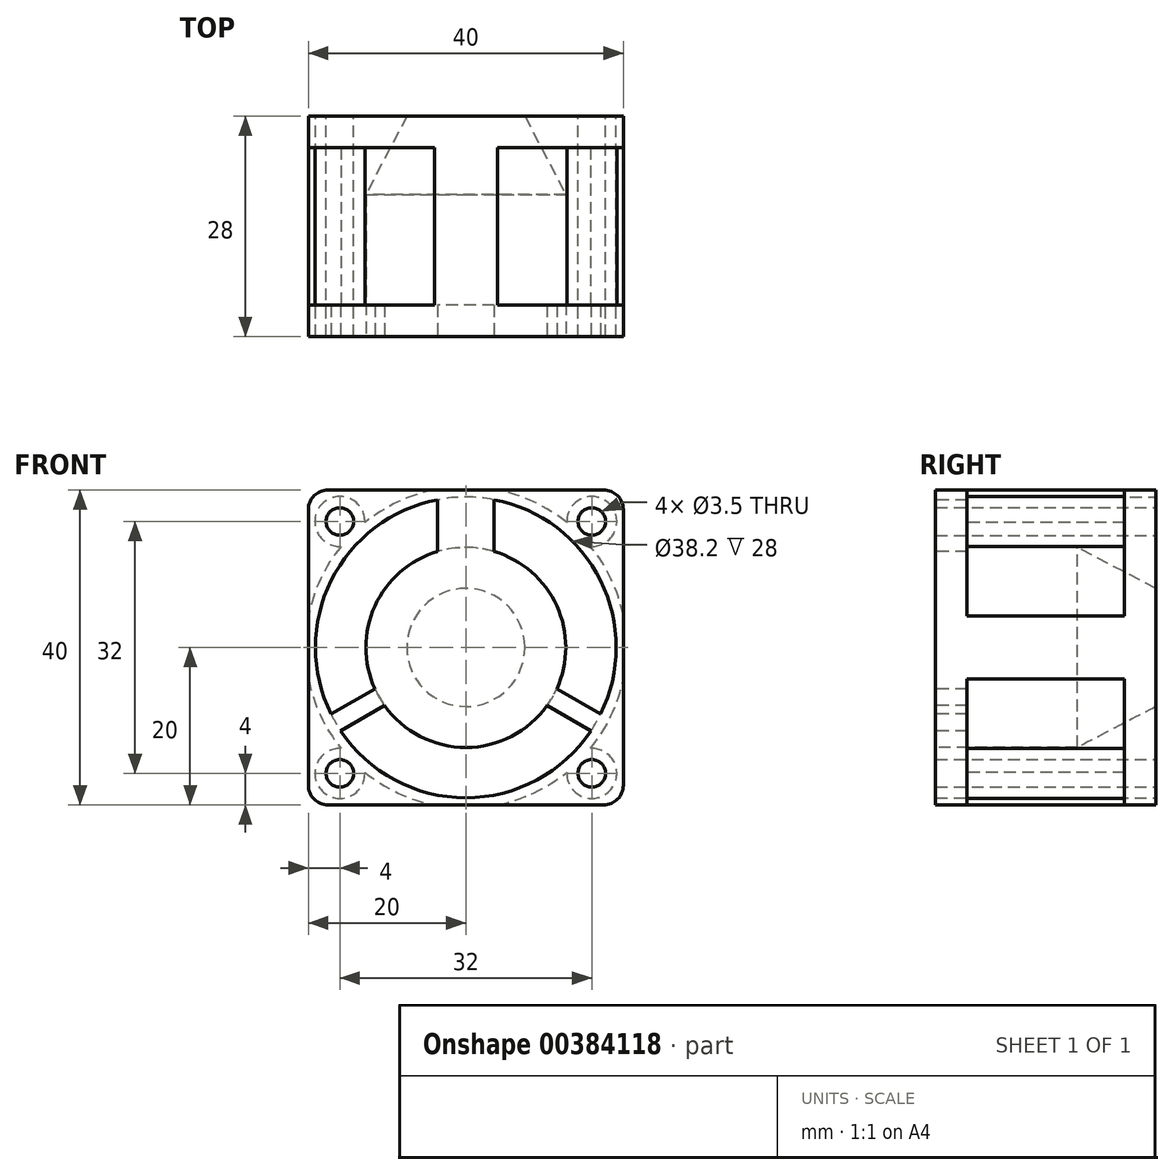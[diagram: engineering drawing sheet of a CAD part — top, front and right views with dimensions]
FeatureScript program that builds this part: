
annotation { "Feature Type Name" : "Feature", "Feature Type Description" : "" }
export const myFeature = defineFeature(function(context is Context, id is Id, definition is map)
    precondition{}
    {
        {
            var Q0;
            Q0=qCreatedBy(makeId("Front.planeOp"),FACE);
            var sketch = newSketch(context, id + "F0", { "sketchPlane" : qUnion([Q0])});
            skLineSegment(sketch, "E0.bottom", {"start": v(-20, 20) * mm, "end": v(20, 20) * mm});
            skLineSegment(sketch, "E0.top", {"start": v(-20, -20) * mm, "end": v(20, -20) * mm});
            skLineSegment(sketch, "E0.left", {"start": v(-20, 20) * mm, "end": v(-20, -20) * mm});
            skLineSegment(sketch, "E0.right", {"start": v(20, 20) * mm, "end": v(20, -20) * mm});
            skLineSegment(sketch, "E1", {"start": v(0, 22.42) * mm, "end": v(0, -25.75) * mm, "construction": true});
            skLineSegment(sketch, "E2", {"start": v(-21.61, 0) * mm, "end": v(23.43, 0) * mm, "construction": true});
            skLineSegment(sketch, "E3", {"start": v(-20.42, 20.42) * mm, "end": v(24.04, -24.04) * mm, "construction": true});
            skLineSegment(sketch, "E4", {"start": v(22.41, 22.41) * mm, "end": v(-20.4, -20.4) * mm, "construction": true});
            skCircle(sketch, "E5", {"center": v(-16, 16) * mm, "radius": 1.75 * mm});
            skCircle(sketch, "E6", {"center": v(16, 16) * mm, "radius": 1.75 * mm});
            skCircle(sketch, "E7", {"center": v(16, -16) * mm, "radius": 1.75 * mm});
            skCircle(sketch, "E8", {"center": v(-16, -16) * mm, "radius": 1.75 * mm});
            skCircle(sketch, "E9", {"center": v(0, 0) * mm, "radius": 19.1 * mm});
            skSolve(sketch);
        }
        {
            var Q0;
            Q0=qSketchRegion(id+"F0",true);
            extrude(context, id + "F1", {"entities" : qUnion([Q0]), "depth" : 28 * mm, "symmetric" : true});
        }
        {
            var Q0;
            Q0=qCreatedBy(makeId("Front.planeOp"),FACE);
            var sketch = newSketch(context, id + "F2", { "sketchPlane" : qUnion([Q0])});
            skArc(sketch, "E10", {"start": v(-12.83, 15.86) * mm, "mid": v(-18.25, 18.25) * mm, "end": v(-15.86, 12.83) * mm});
            skArc(sketch, "E11", {"start": v(-15.86, 12.83) * mm, "mid": v(-18.46, 8.67) * mm, "end": v(-20, 4) * mm});
            skLineSegment(sketch, "E12", {"start": v(20.4, 20.4) * mm, "end": v(4, 20.4) * mm});
            skLineSegment(sketch, "E13", {"start": v(-20.4, 20.4) * mm, "end": v(-20.4, 4) * mm});
            skLineSegment(sketch, "E14", {"start": v(-20.4, -20.4) * mm, "end": v(-4, -20.4) * mm});
            skLineSegment(sketch, "E15", {"start": v(20.4, -20.4) * mm, "end": v(20.4, -4) * mm});
            skArc(sketch, "E16", {"start": v(15.86, 12.83) * mm, "mid": v(18.25, 18.25) * mm, "end": v(12.83, 15.86) * mm});
            skArc(sketch, "E17", {"start": v(12.83, -15.86) * mm, "mid": v(18.25, -18.25) * mm, "end": v(15.86, -12.83) * mm});
            skArc(sketch, "E18", {"start": v(-15.86, -12.83) * mm, "mid": v(-18.25, -18.25) * mm, "end": v(-12.83, -15.86) * mm});
            skArc(sketch, "E19.trimOffspring", {"start": v(12.83, 15.86) * mm, "mid": v(8.67, 18.46) * mm, "end": v(4, 20) * mm});
            skArc(sketch, "E20.trimOffspring", {"start": v(15.86, -12.83) * mm, "mid": v(18.46, -8.67) * mm, "end": v(20, -4) * mm});
            skArc(sketch, "E21.trimOffspring", {"start": v(-12.83, -15.86) * mm, "mid": v(-8.67, -18.46) * mm, "end": v(-4, -20) * mm});
            skLineSegment(sketch, "E22", {"start": v(-20, 4) * mm, "end": v(-20.4, 4) * mm});
            skLineSegment(sketch, "E23", {"start": v(-20, -4) * mm, "end": v(-20.4, -4) * mm});
            skLineSegment(sketch, "E24", {"start": v(20, -4) * mm, "end": v(20.4, -4) * mm});
            skLineSegment(sketch, "E25", {"start": v(-4, -20) * mm, "end": v(-4, -20.4) * mm});
            skArc(sketch, "E26.trimOffspring", {"start": v(-20, -4) * mm, "mid": v(-18.46, -8.67) * mm, "end": v(-15.86, -12.83) * mm});
            skLineSegment(sketch, "E27.trimOffspring", {"start": v(-20.4, -4) * mm, "end": v(-20.4, -20.4) * mm});
            skLineSegment(sketch, "E28.trimOffspring", {"start": v(4, -20.4) * mm, "end": v(20.4, -20.4) * mm});
            skArc(sketch, "E29.trimOffspring", {"start": v(4, -20) * mm, "mid": v(8.67, -18.46) * mm, "end": v(12.83, -15.86) * mm});
            skLineSegment(sketch, "E30.trimOffspring", {"start": v(20.4, 4) * mm, "end": v(20.4, 20.4) * mm});
            skArc(sketch, "E31.trimOffspring", {"start": v(20, 4) * mm, "mid": v(18.46, 8.67) * mm, "end": v(15.86, 12.83) * mm});
            skLineSegment(sketch, "E32.trimOffspring", {"start": v(-4, 20.4) * mm, "end": v(-20.4, 20.4) * mm});
            skArc(sketch, "E33.trimOffspring", {"start": v(-4, 20) * mm, "mid": v(-8.67, 18.46) * mm, "end": v(-12.83, 15.86) * mm});
            skLineSegment(sketch, "E34", {"start": v(4, 20.4) * mm, "end": v(4, 20) * mm});
            skLineSegment(sketch, "E35", {"start": v(-4, 20.4) * mm, "end": v(-4, 20) * mm});
            skLineSegment(sketch, "E36", {"start": v(20, 4) * mm, "end": v(20.4, 4) * mm});
            skLineSegment(sketch, "E37", {"start": v(4, -20.4) * mm, "end": v(4, -20) * mm});
            skSolve(sketch);
        }
        {
            var Q0;
            Q0=qSketchRegion(id+"F2",true);
            extrude(context, id + "F3", {"entities" : qUnion([Q0]), "operationType" : NewBodyOperationType.REMOVE, "oppositeDirection" : true, "depth" : 20 * mm, "symmetric" : true});
        }
        {
            var Q0;
            {var subQ0=sQuery(id+"F0.wireOp",EDGE,"E0.bottom");var subQ1=sQuery(id+"F0.wireOp",EDGE,"E0.right");Q0=makeQuery(id+"F3.boolean.opBoolean","SPLIT",EDGE,{"disambiguationData":[TD([makeQuery(id+"F3.opExtrude","CAP_FACE",FACE,{"disambiguationData":[OSD([sQuery(id+"F2.wireOp",EDGE,"E12"),sQuery(id+"F2.wireOp",EDGE,"E16"),sQuery(id+"F2.wireOp",EDGE,"E19.trimOffspring"),sQuery(id+"F2.wireOp",EDGE,"5qj6X1HE-5dRS-yjT4-1pPR-XCu9oSXyVZGm"),sQuery(id+"F2.wireOp",EDGE,"E24"),sQuery(id+"F2.wireOp",EDGE,"E30.trimOffspring"),sQuery(id+"F2.wireOp",EDGE,"E31.trimOffspring")])],"isStart":true})])],"derivedFrom":makeQuery(id+"F1.opExtrude","SWEPT_EDGE",EDGE,{"disambiguationData":[OSD([subQ0,subQ1])]})});}
            var Q1;
            {var subQ0=sQuery(id+"F0.wireOp",EDGE,"E0.bottom");var subQ1=sQuery(id+"F0.wireOp",EDGE,"E0.right");Q1=makeQuery(id+"F3.boolean.opBoolean","SPLIT",EDGE,{"disambiguationData":[TD([makeQuery(id+"F3.opExtrude","CAP_FACE",FACE,{"disambiguationData":[OSD([sQuery(id+"F2.wireOp",EDGE,"E12"),sQuery(id+"F2.wireOp",EDGE,"E16"),sQuery(id+"F2.wireOp",EDGE,"E19.trimOffspring"),sQuery(id+"F2.wireOp",EDGE,"5qj6X1HE-5dRS-yjT4-1pPR-XCu9oSXyVZGm"),sQuery(id+"F2.wireOp",EDGE,"E24"),sQuery(id+"F2.wireOp",EDGE,"E30.trimOffspring"),sQuery(id+"F2.wireOp",EDGE,"E31.trimOffspring")])],"isStart":false})])],"derivedFrom":makeQuery(id+"F1.opExtrude","SWEPT_EDGE",EDGE,{"disambiguationData":[OSD([subQ0,subQ1])]})});}
            var Q2;
            {var subQ0=sQuery(id+"F0.wireOp",EDGE,"E0.right");var subQ1=sQuery(id+"F0.wireOp",EDGE,"E0.top");Q2=makeQuery(id+"F3.boolean.opBoolean","SPLIT",EDGE,{"disambiguationData":[TD([makeQuery(id+"F3.opExtrude","CAP_FACE",FACE,{"disambiguationData":[OSD([sQuery(id+"F2.wireOp",EDGE,"E15"),sQuery(id+"F2.wireOp",EDGE,"E17"),sQuery(id+"F2.wireOp",EDGE,"E20.trimOffspring"),sQuery(id+"F2.wireOp",EDGE,"E24"),sQuery(id+"F2.wireOp",EDGE,"E25"),sQuery(id+"F2.wireOp",EDGE,"E28.trimOffspring"),sQuery(id+"F2.wireOp",EDGE,"E29.trimOffspring")])],"isStart":true})])],"derivedFrom":makeQuery(id+"F1.opExtrude","SWEPT_EDGE",EDGE,{"disambiguationData":[OSD([subQ1,subQ0])]})});}
            var Q3;
            {var subQ0=sQuery(id+"F0.wireOp",EDGE,"E0.right");var subQ1=sQuery(id+"F0.wireOp",EDGE,"E0.top");Q3=makeQuery(id+"F3.boolean.opBoolean","SPLIT",EDGE,{"disambiguationData":[TD([makeQuery(id+"F3.opExtrude","CAP_FACE",FACE,{"disambiguationData":[OSD([sQuery(id+"F2.wireOp",EDGE,"E15"),sQuery(id+"F2.wireOp",EDGE,"E17"),sQuery(id+"F2.wireOp",EDGE,"E20.trimOffspring"),sQuery(id+"F2.wireOp",EDGE,"E24"),sQuery(id+"F2.wireOp",EDGE,"E25"),sQuery(id+"F2.wireOp",EDGE,"E28.trimOffspring"),sQuery(id+"F2.wireOp",EDGE,"E29.trimOffspring")])],"isStart":false})])],"derivedFrom":makeQuery(id+"F1.opExtrude","SWEPT_EDGE",EDGE,{"disambiguationData":[OSD([subQ1,subQ0])]})});}
            var Q4;
            {var subQ0=sQuery(id+"F0.wireOp",EDGE,"E0.bottom");var subQ1=sQuery(id+"F0.wireOp",EDGE,"E0.left");Q4=makeQuery(id+"F3.boolean.opBoolean","SPLIT",EDGE,{"disambiguationData":[TD([makeQuery(id+"F3.opExtrude","CAP_FACE",FACE,{"disambiguationData":[OSD([sQuery(id+"F2.wireOp",EDGE,"E10"),sQuery(id+"F2.wireOp",EDGE,"E11"),sQuery(id+"F2.wireOp",EDGE,"E13"),sQuery(id+"F2.wireOp",EDGE,"pvrkBk7z-V1rM-OS9Q-dIUC-16UQzA1z2bkd"),sQuery(id+"F2.wireOp",EDGE,"E22"),sQuery(id+"F2.wireOp",EDGE,"E32.trimOffspring"),sQuery(id+"F2.wireOp",EDGE,"E33.trimOffspring")])],"isStart":true})])],"derivedFrom":makeQuery(id+"F1.opExtrude","SWEPT_EDGE",EDGE,{"disambiguationData":[OSD([subQ0,subQ1])]})});}
            var Q5;
            {var subQ0=sQuery(id+"F0.wireOp",EDGE,"E0.bottom");var subQ1=sQuery(id+"F0.wireOp",EDGE,"E0.left");Q5=makeQuery(id+"F3.boolean.opBoolean","SPLIT",EDGE,{"disambiguationData":[TD([makeQuery(id+"F3.opExtrude","CAP_FACE",FACE,{"disambiguationData":[OSD([sQuery(id+"F2.wireOp",EDGE,"E10"),sQuery(id+"F2.wireOp",EDGE,"E11"),sQuery(id+"F2.wireOp",EDGE,"E13"),sQuery(id+"F2.wireOp",EDGE,"pvrkBk7z-V1rM-OS9Q-dIUC-16UQzA1z2bkd"),sQuery(id+"F2.wireOp",EDGE,"E22"),sQuery(id+"F2.wireOp",EDGE,"E32.trimOffspring"),sQuery(id+"F2.wireOp",EDGE,"E33.trimOffspring")])],"isStart":false})])],"derivedFrom":makeQuery(id+"F1.opExtrude","SWEPT_EDGE",EDGE,{"disambiguationData":[OSD([subQ0,subQ1])]})});}
            var Q6;
            {var subQ0=sQuery(id+"F0.wireOp",EDGE,"E0.left");var subQ1=sQuery(id+"F0.wireOp",EDGE,"E0.top");Q6=makeQuery(id+"F3.boolean.opBoolean","SPLIT",EDGE,{"disambiguationData":[TD([makeQuery(id+"F3.opExtrude","CAP_FACE",FACE,{"disambiguationData":[OSD([sQuery(id+"F2.wireOp",EDGE,"E14"),sQuery(id+"F2.wireOp",EDGE,"E18"),sQuery(id+"F2.wireOp",EDGE,"E21.trimOffspring"),sQuery(id+"F2.wireOp",EDGE,"E23"),sQuery(id+"F2.wireOp",EDGE,"E25"),sQuery(id+"F2.wireOp",EDGE,"E26.trimOffspring"),sQuery(id+"F2.wireOp",EDGE,"E27.trimOffspring")])],"isStart":false})])],"derivedFrom":makeQuery(id+"F1.opExtrude","SWEPT_EDGE",EDGE,{"disambiguationData":[OSD([subQ1,subQ0])]})});}
            var Q7;
            {var subQ0=sQuery(id+"F0.wireOp",EDGE,"E0.left");var subQ1=sQuery(id+"F0.wireOp",EDGE,"E0.top");Q7=makeQuery(id+"F3.boolean.opBoolean","SPLIT",EDGE,{"disambiguationData":[TD([makeQuery(id+"F3.opExtrude","CAP_FACE",FACE,{"disambiguationData":[OSD([sQuery(id+"F2.wireOp",EDGE,"E14"),sQuery(id+"F2.wireOp",EDGE,"E18"),sQuery(id+"F2.wireOp",EDGE,"E21.trimOffspring"),sQuery(id+"F2.wireOp",EDGE,"E23"),sQuery(id+"F2.wireOp",EDGE,"E25"),sQuery(id+"F2.wireOp",EDGE,"E26.trimOffspring"),sQuery(id+"F2.wireOp",EDGE,"E27.trimOffspring")])],"isStart":true})])],"derivedFrom":makeQuery(id+"F1.opExtrude","SWEPT_EDGE",EDGE,{"disambiguationData":[OSD([subQ1,subQ0])]})});}
            fillet(context, id + "F4", {"entities" : qUnion([Q0, Q1, Q2, Q3, Q4, Q5, Q6, Q7]), "radius" : 2.5 * mm, "tangentPropagation" : true, "allowEdgeOverflow" : false});
        }
        {
            var Q0;
            Q0=makeQuery(id+"F1.opExtrude","CAP_FACE",FACE,{"disambiguationData":[OSD([sQuery(id+"F0.wireOp",EDGE,"E0.bottom"),sQuery(id+"F0.wireOp",EDGE,"E0.top"),sQuery(id+"F0.wireOp",EDGE,"E0.left"),sQuery(id+"F0.wireOp",EDGE,"E0.right"),sQuery(id+"F0.wireOp",EDGE,"E5"),sQuery(id+"F0.wireOp",EDGE,"E6"),sQuery(id+"F0.wireOp",EDGE,"E7"),sQuery(id+"F0.wireOp",EDGE,"E8"),sQuery(id+"F0.wireOp",EDGE,"E9")])],"isStart":false});
            var sketch = newSketch(context, id + "F5", { "sketchPlane" : qUnion([Q0])});
            skArc(sketch, "E38", {"start": v(-3.6, 12.18) * mm, "mid": v(-11.55, 5.27) * mm, "end": v(-11.56, -5.26) * mm});
            skLineSegment(sketch, "E39", {"start": v(0, 0) * mm, "end": v(0, 20.9) * mm, "construction": true});
            skLineSegment(sketch, "E40.1.0", {"start": v(0, 0) * mm, "end": v(-18.1, -10.45) * mm, "construction": true});
            skLineSegment(sketch, "E40.2.0", {"start": v(0, 0) * mm, "end": v(18.1, -10.45) * mm, "construction": true});
            skLineSegment(sketch, "E41", {"start": v(-3.6, 18.76) * mm, "end": v(-3.6, 12.18) * mm});
            skLineSegment(sketch, "E42", {"start": v(3.6, 12.18) * mm, "end": v(3.6, 18.76) * mm});
            skArc(sketch, "E43", {"start": v(-3.6, 18.76) * mm, "mid": v(0, 19.1) * mm, "end": v(3.6, 18.76) * mm});
            skLineSegment(sketch, "E44", {"start": v(-11.56, -5.26) * mm, "end": v(-17.12, -8.47) * mm});
            skLineSegment(sketch, "E45", {"start": v(-10.33, -7.38) * mm, "end": v(-15.9, -10.6) * mm});
            skLineSegment(sketch, "E46", {"start": v(10.33, -7.38) * mm, "end": v(15.9, -10.6) * mm});
            skLineSegment(sketch, "E47", {"start": v(11.56, -5.26) * mm, "end": v(17.12, -8.47) * mm});
            skArc(sketch, "E48.trimOffspring", {"start": v(-10.33, -7.38) * mm, "mid": v(0, -12.7) * mm, "end": v(10.33, -7.38) * mm});
            skArc(sketch, "E49.trimOffspring", {"start": v(11.56, -5.26) * mm, "mid": v(11.55, 5.27) * mm, "end": v(3.6, 12.18) * mm});
            skArc(sketch, "E50", {"start": v(-17.12, -8.47) * mm, "mid": v(-16.54, -9.55) * mm, "end": v(-15.9, -10.6) * mm});
            skArc(sketch, "E51", {"start": v(17.12, -8.47) * mm, "mid": v(16.54, -9.55) * mm, "end": v(15.9, -10.6) * mm});
            skSolve(sketch);
        }
        {
            var Q0;
            Q0 = qSketchRegion(id + "F5", true);
            extrude(context, id + "F6", {"entities" : qUnion([Q0]), "operationType" : NewBodyOperationType.ADD, "oppositeDirection" : true, "depth" : 4 * mm});
        }
        {
            var Q0;
            Q0=qCreatedBy(makeId("Right.planeOp"),FACE);
            var sketch = newSketch(context, id + "F7", { "sketchPlane" : qUnion([Q0])});
            skLineSegment(sketch, "E52", {"start": v(14, 0) * mm, "end": v(14, 7.5) * mm});
            skLineSegment(sketch, "E53", {"start": v(14, 7.5) * mm, "end": v(4, 12.7) * mm});
            skLineSegment(sketch, "E54", {"start": v(4, 12.7) * mm, "end": v(-10, 12.7) * mm});
            skLineSegment(sketch, "E55", {"start": v(-10, 12.7) * mm, "end": v(-10, 0) * mm});
            skLineSegment(sketch, "E56", {"start": v(-10, 0) * mm, "end": v(14, 0) * mm});
            skLineSegment(sketch, "E57", {"start": v(-15.88, 0) * mm, "end": v(18.33, 0) * mm, "construction": true});
            skSolve(sketch);
        }
        {
            var Q0;
            Q0 = qSketchRegion(id + "F7", true);
            var Q1;
            Q1=sQuery(id+"F7.wireOp",EDGE,"E57");
            revolve(context, id + "F8", {"operationType" : NewBodyOperationType.ADD, "entities" : qUnion([Q0]), "axis" : qUnion([Q1]), "revolveType" : RevolveType.FULL});
        }
    });
